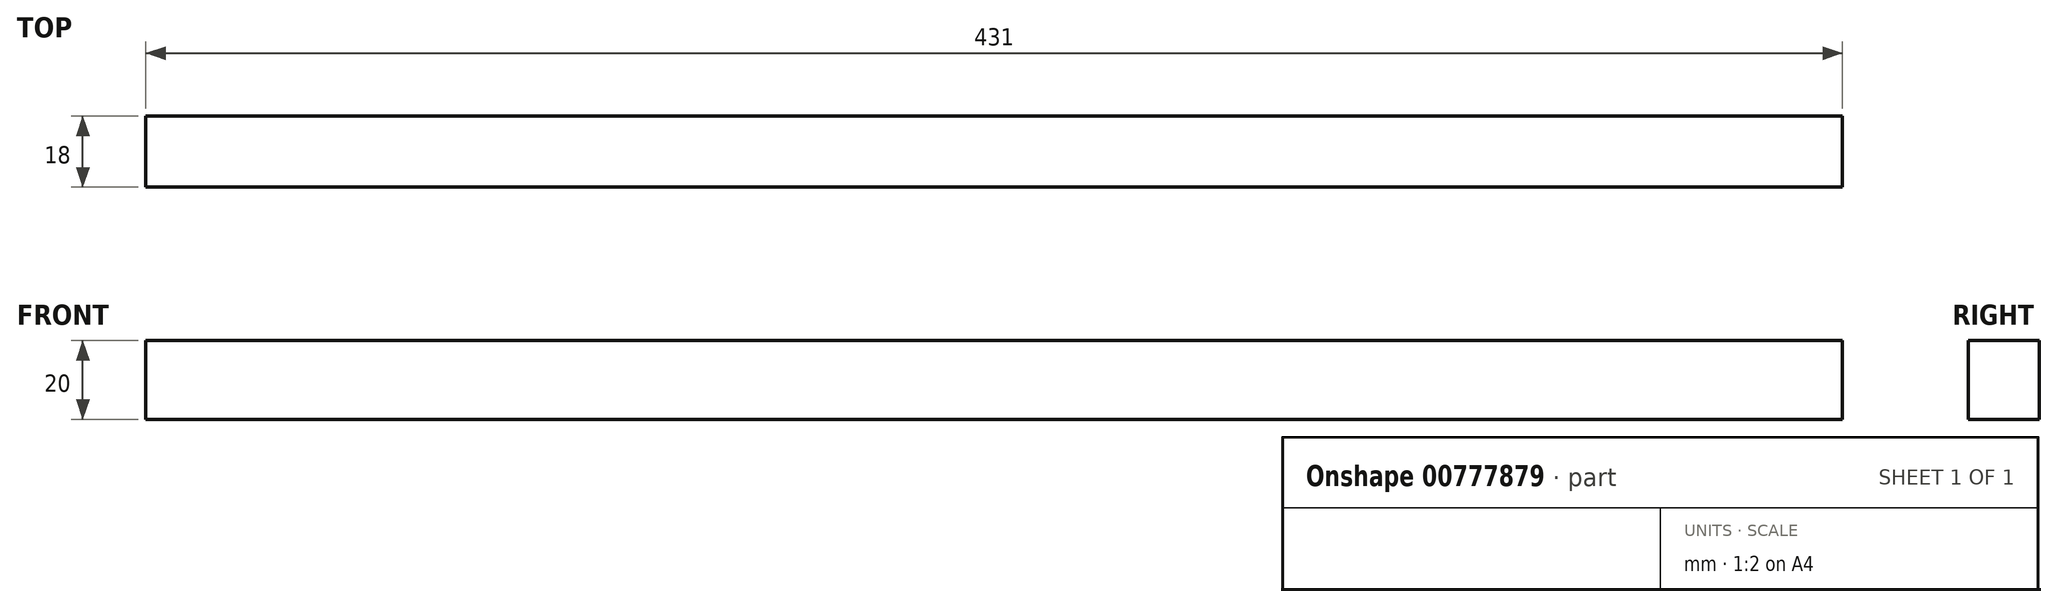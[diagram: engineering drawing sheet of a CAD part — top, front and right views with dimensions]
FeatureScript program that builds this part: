
annotation { "Feature Type Name" : "Feature", "Feature Type Description" : "" }
export const myFeature = defineFeature(function(context is Context, id is Id, definition is map)
    precondition{}
    {
        {
            var Q0;
            Q0=qCreatedBy(makeId("Top.planeOp"),FACE);
            var sketch = newSketch(context, id + "F0", { "sketchPlane" : qUnion([Q0])});
            skLineSegment(sketch, "E0.bottom", {"start": v(-215.5, 9) * mm, "end": v(215.5, 9) * mm});
            skLineSegment(sketch, "E0.top", {"start": v(-215.5, -9) * mm, "end": v(215.5, -9) * mm});
            skLineSegment(sketch, "E0.left", {"start": v(-215.5, 9) * mm, "end": v(-215.5, -9) * mm});
            skLineSegment(sketch, "E0.right", {"start": v(215.5, 9) * mm, "end": v(215.5, -9) * mm});
            skSolve(sketch);
        }
        {
            var Q0;
            Q0 = qSketchRegion(id + "F0", true);
            extrude(context, id + "F1", {"entities" : qUnion([Q0]), "endBound" : BoundingType.SYMMETRIC, "depth" : 20 * mm, "offsetDistance" : 25 * mm});
        }
    });
